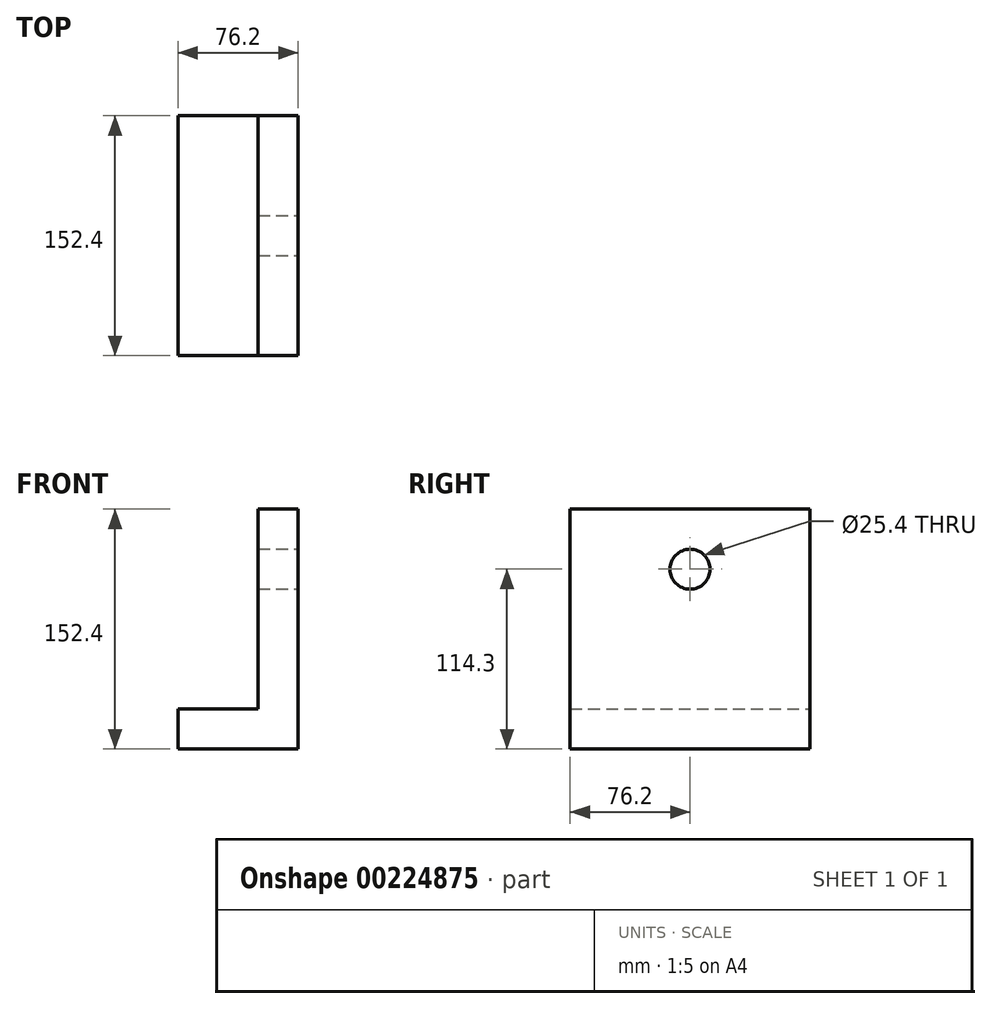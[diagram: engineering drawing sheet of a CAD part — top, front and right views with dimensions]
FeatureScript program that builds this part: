
annotation { "Feature Type Name" : "Feature", "Feature Type Description" : "" }
export const myFeature = defineFeature(function(context is Context, id is Id, definition is map)
    precondition{}
    {
        {
            var Q0;
            Q0=qCreatedBy(makeId("Front.planeOp"),FACE);
            var sketch = newSketch(context, id + "F0", { "sketchPlane" : qUnion([Q0])});
            skLineSegment(sketch, "E0", {"start": v(0, 0) * mm, "end": v(-76.2, 0) * mm});
            skLineSegment(sketch, "E1", {"start": v(0, 0) * mm, "end": v(0, 152.4) * mm});
            skLineSegment(sketch, "E2", {"start": v(0, 152.4) * mm, "end": v(-25.4, 152.4) * mm});
            skLineSegment(sketch, "E3", {"start": v(-25.4, 152.4) * mm, "end": v(-25.4, 25.4) * mm});
            skLineSegment(sketch, "E4", {"start": v(-25.4, 25.4) * mm, "end": v(-76.2, 25.4) * mm});
            skLineSegment(sketch, "E5", {"start": v(-76.2, 25.4) * mm, "end": v(-76.2, 0) * mm});
            skSolve(sketch);
        }
        {
            var Q0;
            Q0 = qSketchRegion(id + "F0", true);
            extrude(context, id + "F1", {"entities" : qUnion([Q0]), "endBound" : BoundingType.SYMMETRIC, "depth" : 152.4 * mm});
        }
        {
            var Q0;
            Q0=makeQuery(id+"F1.opExtrude","SWEPT_FACE",FACE,{"disambiguationData":[OSD([sQuery(id+"F0.wireOp",EDGE,"E1")])]});
            var sketch = newSketch(context, id + "F2", { "sketchPlane" : qUnion([Q0])});
            skCircle(sketch, "E6", {"center": v(0, 114.3) * mm, "radius": 12.7 * mm});
            skSolve(sketch);
        }
        {
            var Q0;
            Q0=makeQuery(id+"F2.imprint","IMPRINT",FACE,{"disambiguationData":[TD([[makeQuery(id+"F2.imprint","IMPRINT",EDGE,{"derivedFrom":sQuery(id+"F2.wireOp",EDGE,"E6")}),1.0]])]});
            extrude(context, id + "F3", {"entities" : qUnion([Q0]), "operationType" : NewBodyOperationType.REMOVE, "endBound" : BoundingType.THROUGH_ALL, "oppositeDirection" : true, "depth" : 25.4 * mm});
        }
    });
